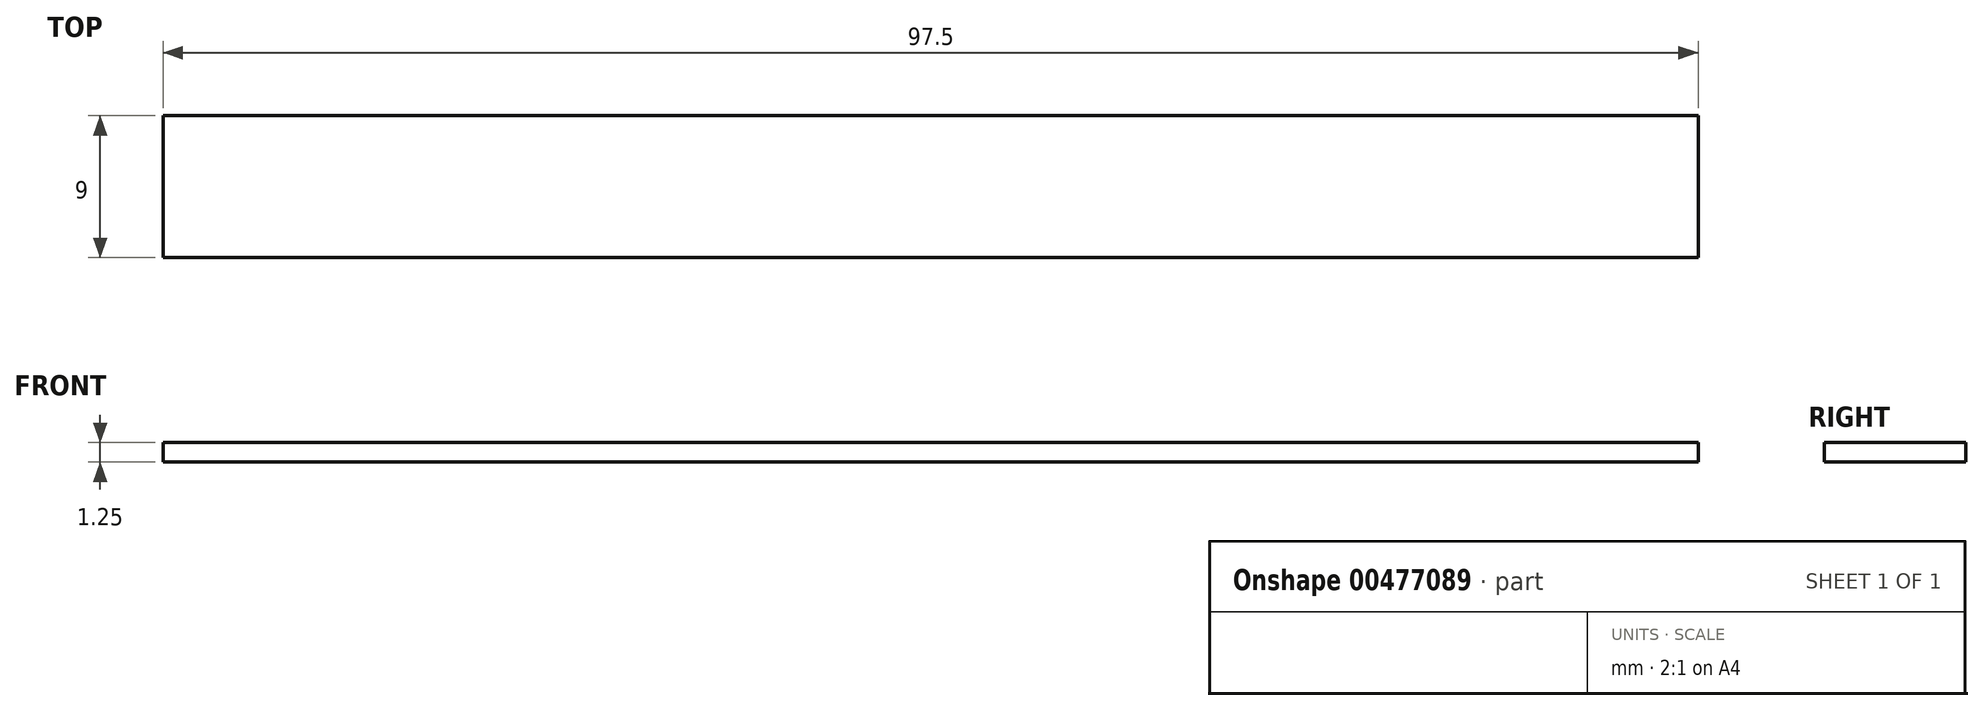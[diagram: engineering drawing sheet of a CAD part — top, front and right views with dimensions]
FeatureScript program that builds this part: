
annotation { "Feature Type Name" : "Feature", "Feature Type Description" : "" }
export const myFeature = defineFeature(function(context is Context, id is Id, definition is map)
    precondition{}
    {
        {
            var Q0;
            Q0=qCreatedBy(makeId("Top.planeOp"),FACE);
            var sketch = newSketch(context, id + "F0", { "sketchPlane" : qUnion([Q0])});
            skLineSegment(sketch, "E0.bottom", {"start": v(-49.98, -5.76) * mm, "end": v(47.52, -5.76) * mm});
            skLineSegment(sketch, "E0.top", {"start": v(-49.98, -14.76) * mm, "end": v(47.52, -14.76) * mm});
            skLineSegment(sketch, "E0.left", {"start": v(-49.98, -5.76) * mm, "end": v(-49.98, -14.76) * mm});
            skLineSegment(sketch, "E0.right", {"start": v(47.52, -5.76) * mm, "end": v(47.52, -14.76) * mm});
            skSolve(sketch);
        }
        {
            var Q0;
            Q0=qSketchRegion(id+"F0",true);
            extrude(context, id + "F1", {"entities" : qUnion([Q0]), "depth" : 1.25 * mm});
        }
    });
